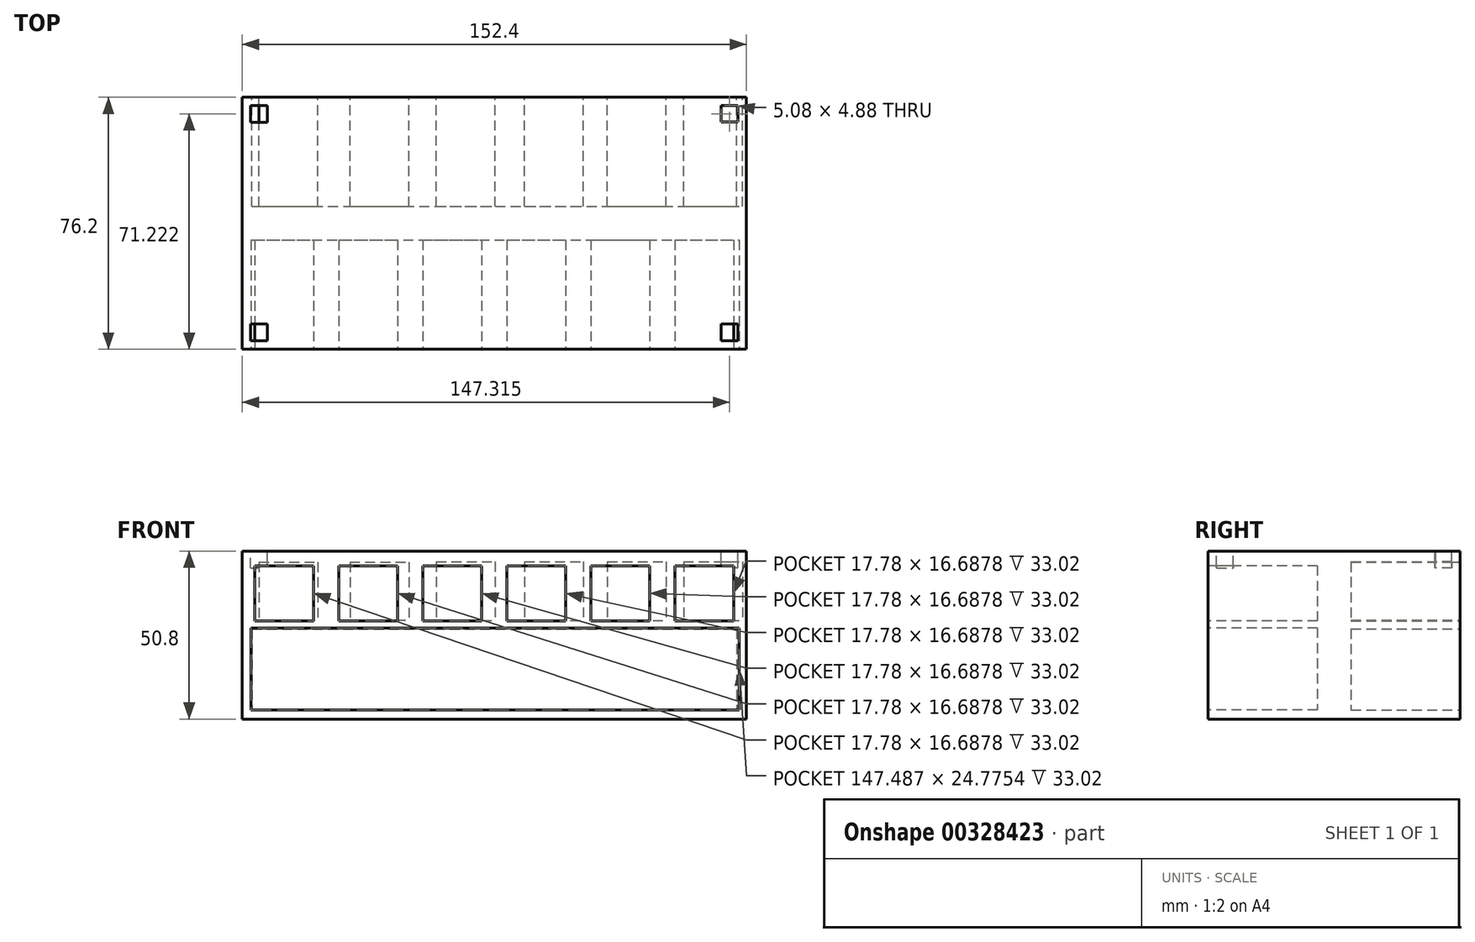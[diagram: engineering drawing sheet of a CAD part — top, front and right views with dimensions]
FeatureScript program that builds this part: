
annotation { "Feature Type Name" : "Feature", "Feature Type Description" : "" }
export const myFeature = defineFeature(function(context is Context, id is Id, definition is map)
    precondition{}
    {
        {
            var Q0;
            Q0=qCreatedBy(makeId("Front.planeOp"),FACE);
            var sketch = newSketch(context, id + "F0", { "sketchPlane" : qUnion([Q0])});
            skLineSegment(sketch, "E0.bottom", {"start": v(-82.48, 50.8) * mm, "end": v(69.92, 50.8) * mm});
            skLineSegment(sketch, "E0.top", {"start": v(-82.48, 0) * mm, "end": v(69.92, 0) * mm});
            skLineSegment(sketch, "E0.left", {"start": v(-82.48, 50.8) * mm, "end": v(-82.48, 0) * mm});
            skLineSegment(sketch, "E0.right", {"start": v(69.92, 50.8) * mm, "end": v(69.92, 0) * mm});
            skLineSegment(sketch, "E1.bottom", {"start": v(-82.48, 25.4) * mm, "end": v(69.92, 25.4) * mm});
            skLineSegment(sketch, "E1.top", {"start": v(-82.48, 25.4) * mm, "end": v(69.92, 25.4) * mm});
            skLineSegment(sketch, "E1.left", {"start": v(-82.48, 25.4) * mm, "end": v(-82.48, 25.4) * mm});
            skLineSegment(sketch, "E1.right", {"start": v(69.92, 25.4) * mm, "end": v(69.92, 25.4) * mm});
            skSolve(sketch);
        }
        {
            var Q0;
            Q0 = qSketchRegion(id + "F0", true);
            extrude(context, id + "F1", {"entities" : qUnion([Q0]), "depth" : 76.2 * mm});
        }
        {
            var Q0;
            Q0=qCreatedBy(makeId("Front.planeOp"),FACE);
            var sketch = newSketch(context, id + "F2", { "sketchPlane" : qUnion([Q0])});
            skLineSegment(sketch, "E2.bottom", {"start": v(-77.42, 47.46) * mm, "end": v(-59.64, 47.46) * mm});
            skLineSegment(sketch, "E2.top", {"start": v(-77.42, 29.68) * mm, "end": v(-59.64, 29.68) * mm});
            skLineSegment(sketch, "E2.left", {"start": v(-77.42, 47.46) * mm, "end": v(-77.42, 29.68) * mm});
            skLineSegment(sketch, "E2.right", {"start": v(-59.64, 47.46) * mm, "end": v(-59.64, 29.68) * mm});
            skLineSegment(sketch, "E3.bottom", {"start": v(-49.92, 47.46) * mm, "end": v(-32.14, 47.46) * mm});
            skLineSegment(sketch, "E3.top", {"start": v(-49.92, 29.96) * mm, "end": v(-32.14, 29.96) * mm});
            skLineSegment(sketch, "E3.left", {"start": v(-49.92, 47.46) * mm, "end": v(-49.92, 29.96) * mm});
            skLineSegment(sketch, "E3.right", {"start": v(-32.14, 47.46) * mm, "end": v(-32.14, 29.96) * mm});
            skLineSegment(sketch, "E4.bottom", {"start": v(-23.8, 47.56) * mm, "end": v(-6.03, 47.56) * mm});
            skLineSegment(sketch, "E4.top", {"start": v(-23.8, 29.78) * mm, "end": v(-6.03, 29.78) * mm});
            skLineSegment(sketch, "E4.left", {"start": v(-23.8, 47.56) * mm, "end": v(-23.8, 29.78) * mm});
            skLineSegment(sketch, "E4.right", {"start": v(-6.03, 47.56) * mm, "end": v(-6.03, 29.78) * mm});
            skPoint(sketch, "E5.firstSnap0", {"position": v(-14.92, 47.56) * mm});
            skLineSegment(sketch, "E5.bottom", {"start": v(2.86, 47.56) * mm, "end": v(20.64, 47.56) * mm});
            skLineSegment(sketch, "E5.top", {"start": v(2.86, 29.78) * mm, "end": v(20.64, 29.78) * mm});
            skLineSegment(sketch, "E5.left", {"start": v(2.86, 47.56) * mm, "end": v(2.86, 29.78) * mm});
            skLineSegment(sketch, "E5.right", {"start": v(20.64, 47.56) * mm, "end": v(20.64, 29.78) * mm});
            skLineSegment(sketch, "E6.bottom", {"start": v(27.87, 47.56) * mm, "end": v(45.65, 47.56) * mm});
            skLineSegment(sketch, "E6.top", {"start": v(27.87, 29.78) * mm, "end": v(45.65, 29.78) * mm});
            skLineSegment(sketch, "E6.left", {"start": v(27.87, 47.56) * mm, "end": v(27.87, 29.78) * mm});
            skLineSegment(sketch, "E6.right", {"start": v(45.65, 47.56) * mm, "end": v(45.65, 29.78) * mm});
            skLineSegment(sketch, "E7.bottom", {"start": v(50.93, 47.56) * mm, "end": v(68.7, 47.56) * mm});
            skLineSegment(sketch, "E7.top", {"start": v(50.93, 29.78) * mm, "end": v(68.7, 29.78) * mm});
            skLineSegment(sketch, "E7.left", {"start": v(50.93, 47.56) * mm, "end": v(50.93, 29.78) * mm});
            skLineSegment(sketch, "E7.right", {"start": v(68.7, 47.56) * mm, "end": v(68.7, 29.78) * mm});
            skSolve(sketch);
        }
        {
            var Q0;
            Q0 = qSketchRegion(id + "F2", true);
            extrude(context, id + "F3", {"entities" : qUnion([Q0]), "operationType" : NewBodyOperationType.REMOVE, "depth" : 33.02 * mm});
        }
        {
            var Q0;
            Q0=makeQuery(id+"F1.opExtrude","CAP_FACE",FACE,{"disambiguationData":[OSD([sQuery(id+"F0.wireOp",EDGE,"E0.bottom"),sQuery(id+"F0.wireOp",EDGE,"E0.top"),sQuery(id+"F0.wireOp",EDGE,"E0.left"),sQuery(id+"F0.wireOp",EDGE,"E0.right")])],"isStart":false});
            var sketch = newSketch(context, id + "F4", { "sketchPlane" : qUnion([Q0])});
            skLineSegment(sketch, "E8.bottom", {"start": v(-78.67, 46.37) * mm, "end": v(-60.9, 46.37) * mm});
            skLineSegment(sketch, "E8.top", {"start": v(-78.67, 29.68) * mm, "end": v(-60.9, 29.68) * mm});
            skLineSegment(sketch, "E8.left", {"start": v(-78.67, 46.37) * mm, "end": v(-78.67, 29.68) * mm});
            skLineSegment(sketch, "E8.right", {"start": v(-60.9, 46.37) * mm, "end": v(-60.9, 29.68) * mm});
            skLineSegment(sketch, "E9.bottom", {"start": v(-53.27, 46.37) * mm, "end": v(-35.5, 46.37) * mm});
            skLineSegment(sketch, "E9.top", {"start": v(-53.27, 29.68) * mm, "end": v(-35.5, 29.68) * mm});
            skLineSegment(sketch, "E9.left", {"start": v(-53.27, 46.37) * mm, "end": v(-53.27, 29.68) * mm});
            skLineSegment(sketch, "E9.right", {"start": v(-35.5, 46.37) * mm, "end": v(-35.5, 29.68) * mm});
            skLineSegment(sketch, "E10.bottom", {"start": v(-27.87, 46.37) * mm, "end": v(-10.1, 46.37) * mm});
            skLineSegment(sketch, "E10.top", {"start": v(-27.87, 29.68) * mm, "end": v(-10.1, 29.68) * mm});
            skLineSegment(sketch, "E10.left", {"start": v(-27.87, 46.37) * mm, "end": v(-27.87, 29.68) * mm});
            skLineSegment(sketch, "E10.right", {"start": v(-10.1, 46.37) * mm, "end": v(-10.1, 29.68) * mm});
            skLineSegment(sketch, "E11.bottom", {"start": v(-2.47, 46.37) * mm, "end": v(15.3, 46.37) * mm});
            skLineSegment(sketch, "E11.top", {"start": v(-2.47, 29.68) * mm, "end": v(15.3, 29.68) * mm});
            skLineSegment(sketch, "E11.left", {"start": v(-2.47, 46.37) * mm, "end": v(-2.47, 29.68) * mm});
            skLineSegment(sketch, "E11.right", {"start": v(15.3, 46.37) * mm, "end": v(15.3, 29.68) * mm});
            skLineSegment(sketch, "E12.bottom", {"start": v(22.93, 46.37) * mm, "end": v(40.7, 46.37) * mm});
            skLineSegment(sketch, "E12.top", {"start": v(22.93, 29.68) * mm, "end": v(40.7, 29.68) * mm});
            skLineSegment(sketch, "E12.left", {"start": v(22.93, 46.37) * mm, "end": v(22.93, 29.68) * mm});
            skLineSegment(sketch, "E12.right", {"start": v(40.7, 46.37) * mm, "end": v(40.7, 29.68) * mm});
            skLineSegment(sketch, "E13.bottom", {"start": v(48.33, 46.37) * mm, "end": v(66.1, 46.37) * mm});
            skLineSegment(sketch, "E13.top", {"start": v(48.33, 29.68) * mm, "end": v(66.1, 29.68) * mm});
            skLineSegment(sketch, "E13.left", {"start": v(48.33, 46.37) * mm, "end": v(48.33, 29.68) * mm});
            skLineSegment(sketch, "E13.right", {"start": v(66.1, 46.37) * mm, "end": v(66.1, 29.68) * mm});
            skSolve(sketch);
        }
        {
            var Q0;
            Q0 = qSketchRegion(id + "F4", true);
            extrude(context, id + "F5", {"entities" : qUnion([Q0]), "operationType" : NewBodyOperationType.REMOVE, "oppositeDirection" : true, "depth" : 33.02 * mm});
        }
        {
            var Q0;
            Q0=qCreatedBy(makeId("Front.planeOp"),FACE);
            var sketch = newSketch(context, id + "F6", { "sketchPlane" : qUnion([Q0])});
            skLineSegment(sketch, "E14.bottom", {"start": v(-79.55, 27.24) * mm, "end": v(67, 27.24) * mm});
            skLineSegment(sketch, "E14.top", {"start": v(-79.55, 2.76) * mm, "end": v(67, 2.76) * mm});
            skLineSegment(sketch, "E14.left", {"start": v(-79.55, 27.24) * mm, "end": v(-79.55, 2.76) * mm});
            skLineSegment(sketch, "E14.right", {"start": v(67, 27.24) * mm, "end": v(67, 2.76) * mm});
            skSolve(sketch);
        }
        {
            var Q0;
            Q0 = qSketchRegion(id + "F6", true);
            extrude(context, id + "F7", {"entities" : qUnion([Q0]), "operationType" : NewBodyOperationType.REMOVE, "depth" : 33.02 * mm});
        }
        {
            var Q0;
            Q0=makeQuery(id+"F1.opExtrude","CAP_FACE",FACE,{"disambiguationData":[OSD([sQuery(id+"F0.wireOp",EDGE,"E0.bottom"),sQuery(id+"F0.wireOp",EDGE,"E0.top"),sQuery(id+"F0.wireOp",EDGE,"E0.left"),sQuery(id+"F0.wireOp",EDGE,"E0.right")])],"isStart":false});
            var sketch = newSketch(context, id + "F8", { "sketchPlane" : qUnion([Q0])});
            skLineSegment(sketch, "E15.bottom", {"start": v(-79.8, 27.54) * mm, "end": v(67.69, 27.54) * mm});
            skLineSegment(sketch, "E15.top", {"start": v(-79.8, 2.77) * mm, "end": v(67.69, 2.77) * mm});
            skLineSegment(sketch, "E15.left", {"start": v(-79.8, 27.54) * mm, "end": v(-79.8, 2.77) * mm});
            skLineSegment(sketch, "E15.right", {"start": v(67.69, 27.54) * mm, "end": v(67.69, 2.77) * mm});
            skSolve(sketch);
        }
        {
            var Q0;
            Q0=qCreatedBy(makeId("Front.planeOp"),FACE);
            var sketch = newSketch(context, id + "F9", { "sketchPlane" : qUnion([Q0])});
            skLineSegment(sketch, "E16.bottom", {"start": v(67.1, 27.54) * mm, "end": v(-79.5, 27.54) * mm});
            skLineSegment(sketch, "E16.top", {"start": v(67.1, 2.77) * mm, "end": v(-79.5, 2.77) * mm});
            skLineSegment(sketch, "E16.left", {"start": v(67.1, 27.54) * mm, "end": v(67.1, 2.77) * mm});
            skLineSegment(sketch, "E16.right", {"start": v(-79.5, 27.54) * mm, "end": v(-79.5, 2.77) * mm});
            skSolve(sketch);
        }
        {
            var Q0;
            Q0=makeQuery(id+"F8.imprint","IMPRINT",FACE,{"disambiguationData":[TD([[makeQuery(id+"F8.imprint","IMPRINT",EDGE,{"derivedFrom":sQuery(id+"F8.wireOp",EDGE,"E15.bottom")}),-1.0]])]});
            extrude(context, id + "F10", {"entities" : qUnion([Q0]), "operationType" : NewBodyOperationType.REMOVE, "oppositeDirection" : true, "depth" : 33.02 * mm});
        }
        {
            var Q0;
            Q0=makeQuery(id+"F1.opExtrude","SWEPT_FACE",FACE,{"disambiguationData":[OSD([sQuery(id+"F0.wireOp",EDGE,"E0.bottom")])]});
            var sketch = newSketch(context, id + "F11", { "sketchPlane" : qUnion([Q0])});
            skLineSegment(sketch, "E17.bottom", {"start": v(-79.94, -2.54) * mm, "end": v(-74.86, -2.54) * mm});
            skLineSegment(sketch, "E17.top", {"start": v(-79.94, -7.62) * mm, "end": v(-74.86, -7.62) * mm});
            skLineSegment(sketch, "E17.left", {"start": v(-79.94, -2.54) * mm, "end": v(-79.94, -7.62) * mm});
            skLineSegment(sketch, "E17.right", {"start": v(-74.86, -2.54) * mm, "end": v(-74.86, -7.62) * mm});
            skLineSegment(sketch, "E18.bottom", {"start": v(62.3, -2.54) * mm, "end": v(67.38, -2.54) * mm});
            skLineSegment(sketch, "E18.top", {"start": v(62.3, -7.42) * mm, "end": v(67.38, -7.42) * mm});
            skLineSegment(sketch, "E18.left", {"start": v(62.3, -2.54) * mm, "end": v(62.3, -7.42) * mm});
            skLineSegment(sketch, "E18.right", {"start": v(67.38, -2.54) * mm, "end": v(67.38, -7.42) * mm});
            skLineSegment(sketch, "E19.bottom", {"start": v(67.38, -73.66) * mm, "end": v(62.3, -73.66) * mm});
            skLineSegment(sketch, "E19.top", {"start": v(67.38, -68.58) * mm, "end": v(62.3, -68.58) * mm});
            skLineSegment(sketch, "E19.left", {"start": v(67.38, -73.66) * mm, "end": v(67.38, -68.58) * mm});
            skLineSegment(sketch, "E19.right", {"start": v(62.3, -73.66) * mm, "end": v(62.3, -68.58) * mm});
            skLineSegment(sketch, "E20.bottom", {"start": v(-79.94, -73.66) * mm, "end": v(-74.86, -73.66) * mm});
            skLineSegment(sketch, "E20.top", {"start": v(-79.94, -68.58) * mm, "end": v(-74.86, -68.58) * mm});
            skLineSegment(sketch, "E20.left", {"start": v(-79.94, -73.66) * mm, "end": v(-79.94, -68.58) * mm});
            skLineSegment(sketch, "E20.right", {"start": v(-74.86, -73.66) * mm, "end": v(-74.86, -68.58) * mm});
            skSolve(sketch);
        }
        {
            var Q0;
            Q0 = qSketchRegion(id + "F11", true);
            extrude(context, id + "F12", {"entities" : qUnion([Q0]), "operationType" : NewBodyOperationType.REMOVE, "oppositeDirection" : true, "depth" : 5.08 * mm});
        }
    });
